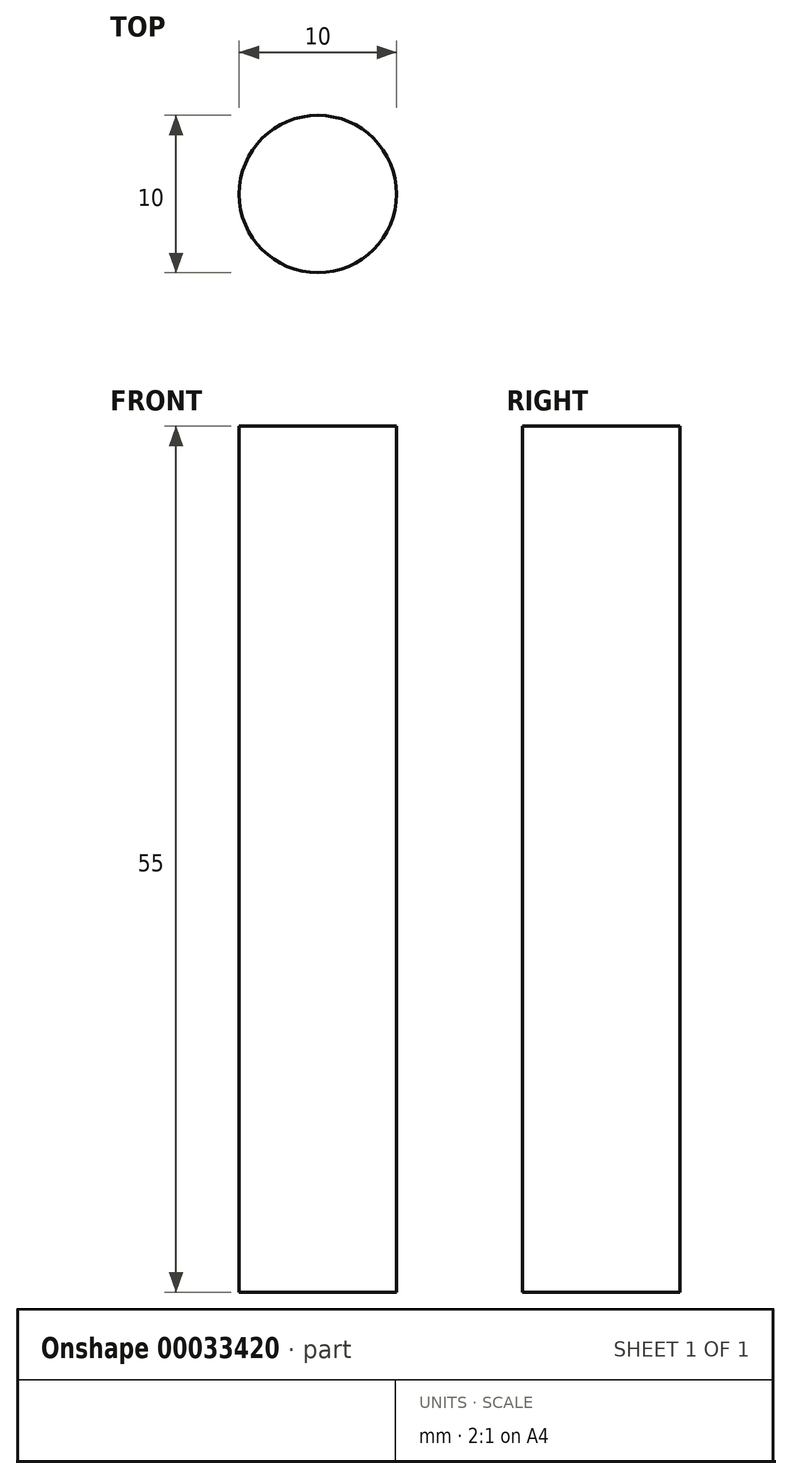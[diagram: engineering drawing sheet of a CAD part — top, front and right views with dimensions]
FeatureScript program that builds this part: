
annotation { "Feature Type Name" : "Feature", "Feature Type Description" : "" }
export const myFeature = defineFeature(function(context is Context, id is Id, definition is map)
    precondition{}
    {
        {
            var Q0;
            Q0=qCreatedBy(makeId("Top.planeOp"),FACE);
            var sketch = newSketch(context, id + "F0", { "sketchPlane" : qUnion([Q0])});
            skCircle(sketch, "E0", {"center": v(0, 0) * mm, "radius": 5 * mm});
            skSolve(sketch);
        }
        {
            var Q0;
            Q0 = qSketchRegion(id + "F0", true);
            extrude(context, id + "F1", {"entities" : qUnion([Q0]), "depth" : 55 * mm});
        }
    });
